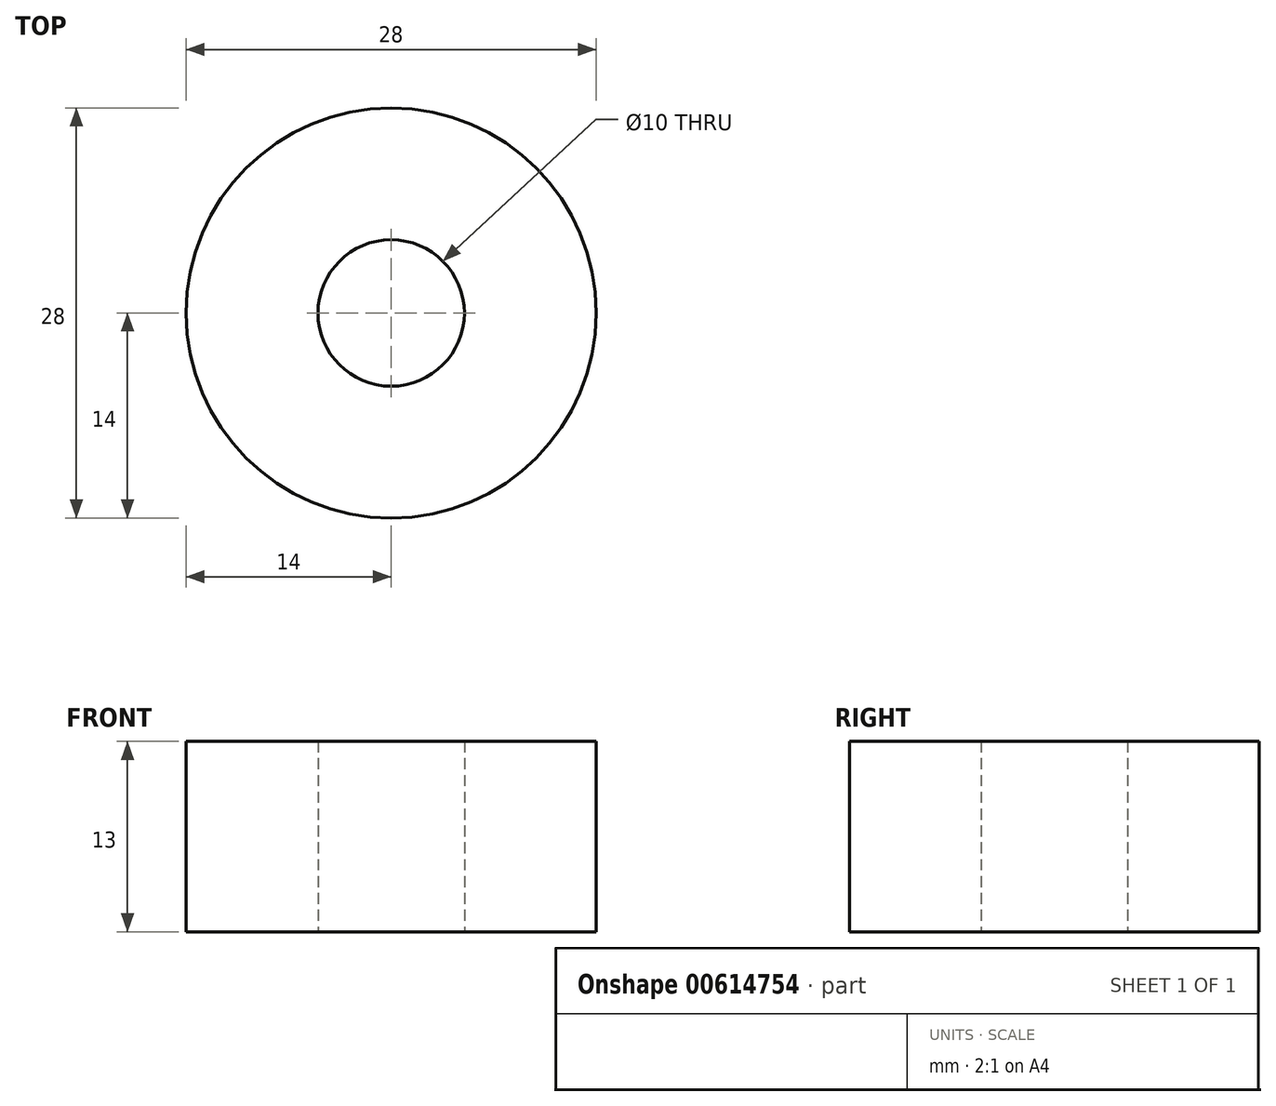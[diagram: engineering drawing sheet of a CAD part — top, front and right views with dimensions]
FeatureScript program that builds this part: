
annotation { "Feature Type Name" : "Feature", "Feature Type Description" : "" }
export const myFeature = defineFeature(function(context is Context, id is Id, definition is map)
    precondition{}
    {
        {
            var Q0;
            Q0=qCreatedBy(makeId("Top.planeOp"),FACE);
            var sketch = newSketch(context, id + "F0", { "sketchPlane" : qUnion([Q0])});
            skCircle(sketch, "E0", {"center": v(0, 0) * mm, "radius": 14 * mm});
            skCircle(sketch, "E1", {"center": v(0, 0) * mm, "radius": 5 * mm});
            skSolve(sketch);
        }
        {
            var Q0;
            Q0=makeQuery(id+"F0.imprint","IMPRINT",FACE,{"disambiguationData":[TD([[makeQuery(id+"F0.imprint","IMPRINT",EDGE,{"derivedFrom":sQuery(id+"F0.wireOp",EDGE,"E0")}),1.0]])]});
            extrude(context, id + "F1", {"entities" : qUnion([Q0]), "depth" : 13 * mm, "offsetDistance" : 25 * mm});
        }
    });
